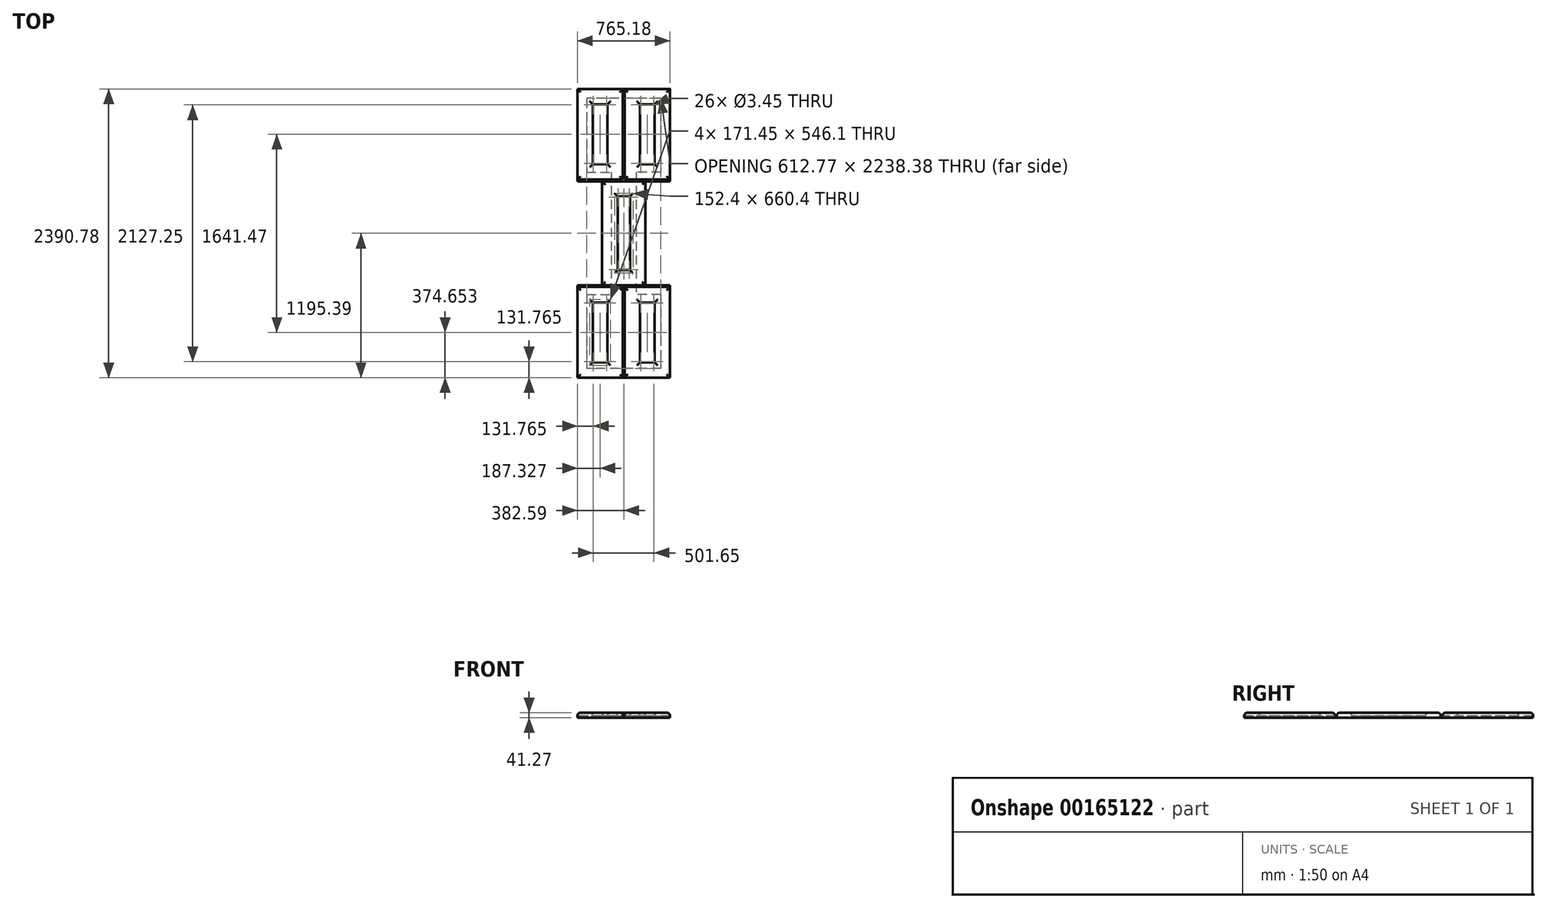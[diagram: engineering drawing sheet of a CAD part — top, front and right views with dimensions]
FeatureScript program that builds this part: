
annotation { "Feature Type Name" : "Feature", "Feature Type Description" : "" }
export const myFeature = defineFeature(function(context is Context, id is Id, definition is map)
    precondition{}
    {
        {
            var Q0;
            Q0=qCreatedBy(makeId("Top.planeOp"),FACE);
            var sketch = newSketch(context, id + "F0", { "sketchPlane" : qUnion([Q0])});
            skLineSegment(sketch, "E0", {"start": v(-179.39, 0) * mm, "end": v(179.39, 0) * mm, "construction": true});
            skLineSegment(sketch, "E1.left", {"start": v(-179.39, -430.21) * mm, "end": v(-179.39, 430.21) * mm});
            skLineSegment(sketch, "E1.right", {"start": v(179.39, -430.21) * mm, "end": v(179.39, 430.21) * mm});
            skLineSegment(sketch, "E2.bottom", {"start": v(-179.39, 430.21) * mm, "end": v(-382.59, 430.21) * mm});
            skLineSegment(sketch, "E2.top", {"start": v(382.59, 1195.39) * mm, "end": v(-382.59, 1195.39) * mm});
            skLineSegment(sketch, "E2.left", {"start": v(382.59, 430.21) * mm, "end": v(382.59, 1195.39) * mm});
            skLineSegment(sketch, "E2.right", {"start": v(-382.59, 430.21) * mm, "end": v(-382.59, 1195.39) * mm});
            skLineSegment(sketch, "E3", {"start": v(0, 0) * mm, "end": v(0, 1195.39) * mm, "construction": true});
            skLineSegment(sketch, "E4", {"start": v(-179.39, -430.21) * mm, "end": v(-382.59, -430.21) * mm});
            skLineSegment(sketch, "E5", {"start": v(179.39, 430.21) * mm, "end": v(382.59, 430.21) * mm});
            skLineSegment(sketch, "E6.bottom", {"start": v(382.59, -1195.39) * mm, "end": v(-382.59, -1195.39) * mm});
            skLineSegment(sketch, "E6.top", {"start": v(382.59, -430.21) * mm, "end": v(179.39, -430.21) * mm});
            skLineSegment(sketch, "E6.left", {"start": v(382.59, -1195.39) * mm, "end": v(382.59, -430.21) * mm});
            skLineSegment(sketch, "E6.right", {"start": v(-382.59, -1195.39) * mm, "end": v(-382.59, -430.21) * mm});
            skLineSegment(sketch, "E7", {"start": v(0, 0) * mm, "end": v(0, -1195.39) * mm, "construction": true});
            skLineSegment(sketch, "E8.bottom", {"start": v(-46.04, -300.04) * mm, "end": v(46.04, -300.04) * mm, "construction": true});
            skLineSegment(sketch, "E8.top", {"start": v(-46.04, 300.04) * mm, "end": v(46.04, 300.04) * mm, "construction": true});
            skLineSegment(sketch, "E8.left", {"start": v(-46.04, -300.04) * mm, "end": v(-46.04, 300.04) * mm, "construction": true});
            skLineSegment(sketch, "E8.right", {"start": v(46.04, -300.04) * mm, "end": v(46.04, 300.04) * mm, "construction": true});
            skPoint(sketch, "E8.middle", {"position": v(0, 0) * mm});
            skCircle(sketch, "E9", {"center": v(-46.04, 300.04) * mm, "radius": 1.73 * mm});
            skCircle(sketch, "E10", {"center": v(46.04, 300.04) * mm, "radius": 1.73 * mm});
            skCircle(sketch, "E11", {"center": v(46.04, 0) * mm, "radius": 1.73 * mm});
            skCircle(sketch, "E12", {"center": v(-46.04, 0) * mm, "radius": 1.73 * mm});
            skCircle(sketch, "E13", {"center": v(-46.04, -300.04) * mm, "radius": 1.73 * mm});
            skCircle(sketch, "E14", {"center": v(46.04, -300.04) * mm, "radius": 1.73 * mm});
            skLineSegment(sketch, "E15", {"start": v(195.26, 1195.39) * mm, "end": v(195.26, 820.74) * mm, "construction": true});
            skLineSegment(sketch, "E16", {"start": v(195.26, 820.74) * mm, "end": v(382.59, 820.74) * mm, "construction": true});
            skLineSegment(sketch, "E17", {"start": v(-195.26, 1195.39) * mm, "end": v(-195.26, 820.74) * mm, "construction": true});
            skLineSegment(sketch, "E18", {"start": v(-195.26, 820.74) * mm, "end": v(-382.59, 820.74) * mm, "construction": true});
            skLineSegment(sketch, "E19.bottom", {"start": v(250.83, 1063.62) * mm, "end": v(139.7, 1063.62) * mm, "construction": true});
            skLineSegment(sketch, "E19.top", {"start": v(250.83, 577.85) * mm, "end": v(139.7, 577.85) * mm, "construction": true});
            skLineSegment(sketch, "E19.left", {"start": v(250.83, 1063.62) * mm, "end": v(250.83, 577.85) * mm, "construction": true});
            skLineSegment(sketch, "E19.right", {"start": v(139.7, 1063.62) * mm, "end": v(139.7, 577.85) * mm, "construction": true});
            skPoint(sketch, "E19.middle", {"position": v(195.26, 820.74) * mm});
            skCircle(sketch, "E20", {"center": v(139.7, 1063.62) * mm, "radius": 1.73 * mm});
            skCircle(sketch, "E21", {"center": v(250.83, 1063.62) * mm, "radius": 1.73 * mm});
            skCircle(sketch, "E22", {"center": v(139.7, 577.85) * mm, "radius": 1.73 * mm});
            skCircle(sketch, "E23", {"center": v(250.83, 577.85) * mm, "radius": 1.73 * mm});
            skCircle(sketch, "E24", {"center": v(195.26, 820.74) * mm, "radius": 1.73 * mm});
            skLineSegment(sketch, "E25.bottom", {"start": v(-139.7, 1063.62) * mm, "end": v(-250.83, 1063.62) * mm, "construction": true});
            skLineSegment(sketch, "E25.top", {"start": v(-139.7, 577.85) * mm, "end": v(-250.83, 577.85) * mm, "construction": true});
            skLineSegment(sketch, "E25.left", {"start": v(-139.7, 1063.62) * mm, "end": v(-139.7, 577.85) * mm, "construction": true});
            skLineSegment(sketch, "E25.right", {"start": v(-250.83, 1063.62) * mm, "end": v(-250.83, 577.85) * mm, "construction": true});
            skPoint(sketch, "E25.middle", {"position": v(-195.26, 820.74) * mm});
            skCircle(sketch, "E26", {"center": v(-250.83, 1063.62) * mm, "radius": 1.73 * mm});
            skCircle(sketch, "E27", {"center": v(-139.7, 1063.62) * mm, "radius": 1.73 * mm});
            skCircle(sketch, "E28", {"center": v(-195.26, 820.74) * mm, "radius": 1.73 * mm});
            skCircle(sketch, "E29", {"center": v(-139.7, 577.85) * mm, "radius": 1.73 * mm});
            skCircle(sketch, "E30", {"center": v(-250.83, 577.85) * mm, "radius": 1.73 * mm});
            skLineSegment(sketch, "E31", {"start": v(-195.26, -1195.39) * mm, "end": v(-195.26, -820.74) * mm, "construction": true});
            skLineSegment(sketch, "E32", {"start": v(-195.26, -820.74) * mm, "end": v(-382.59, -820.74) * mm, "construction": true});
            skLineSegment(sketch, "E33", {"start": v(195.26, -1195.39) * mm, "end": v(195.26, -820.74) * mm, "construction": true});
            skLineSegment(sketch, "E34", {"start": v(195.26, -820.74) * mm, "end": v(382.59, -820.74) * mm, "construction": true});
            skLineSegment(sketch, "E35.bottom", {"start": v(-139.7, -577.85) * mm, "end": v(-250.83, -577.85) * mm, "construction": true});
            skLineSegment(sketch, "E35.top", {"start": v(-139.7, -1063.62) * mm, "end": v(-250.83, -1063.62) * mm, "construction": true});
            skLineSegment(sketch, "E35.left", {"start": v(-139.7, -577.85) * mm, "end": v(-139.7, -1063.62) * mm, "construction": true});
            skLineSegment(sketch, "E35.right", {"start": v(-250.83, -577.85) * mm, "end": v(-250.83, -1063.62) * mm, "construction": true});
            skPoint(sketch, "E35.middle", {"position": v(-195.26, -820.74) * mm});
            skLineSegment(sketch, "E36.bottom", {"start": v(139.7, -577.85) * mm, "end": v(250.82, -577.85) * mm, "construction": true});
            skLineSegment(sketch, "E36.top", {"start": v(139.7, -1063.62) * mm, "end": v(250.82, -1063.62) * mm, "construction": true});
            skLineSegment(sketch, "E36.left", {"start": v(139.7, -577.85) * mm, "end": v(139.7, -1063.62) * mm, "construction": true});
            skLineSegment(sketch, "E36.right", {"start": v(250.82, -577.85) * mm, "end": v(250.82, -1063.62) * mm, "construction": true});
            skPoint(sketch, "E36.middle", {"position": v(195.26, -820.74) * mm});
            skCircle(sketch, "E37", {"center": v(-250.83, -577.85) * mm, "radius": 1.73 * mm});
            skCircle(sketch, "E38", {"center": v(-139.7, -577.85) * mm, "radius": 1.73 * mm});
            skCircle(sketch, "E39", {"center": v(-195.26, -820.74) * mm, "radius": 1.73 * mm});
            skCircle(sketch, "E40", {"center": v(-139.7, -1063.62) * mm, "radius": 1.73 * mm});
            skCircle(sketch, "E41", {"center": v(-250.83, -1063.62) * mm, "radius": 1.73 * mm});
            skCircle(sketch, "E42", {"center": v(139.7, -1063.62) * mm, "radius": 1.73 * mm});
            skCircle(sketch, "E43", {"center": v(250.82, -1063.62) * mm, "radius": 1.73 * mm});
            skCircle(sketch, "E44", {"center": v(195.26, -820.74) * mm, "radius": 1.73 * mm});
            skCircle(sketch, "E45", {"center": v(139.7, -577.85) * mm, "radius": 1.73 * mm});
            skCircle(sketch, "E46", {"center": v(250.82, -577.85) * mm, "radius": 1.73 * mm});
            skSolve(sketch);
        }
        {
            var Q0;
            Q0=qSketchRegion(id+"F0",true);
            extrude(context, id + "F1", {"entities" : qUnion([Q0]), "depth" : 15.88 * mm});
        }
        {
            var Q0;
            Q0=makeQuery(id+"F1.opExtrude","CAP_FACE",FACE,{"disambiguationData":[OSD([sQuery(id+"F0.wireOp",EDGE,"E1.left"),sQuery(id+"F0.wireOp",EDGE,"E1.right"),sQuery(id+"F0.wireOp",EDGE,"E2.bottom"),sQuery(id+"F0.wireOp",EDGE,"E2.top"),sQuery(id+"F0.wireOp",EDGE,"E2.left"),sQuery(id+"F0.wireOp",EDGE,"E2.right"),sQuery(id+"F0.wireOp",EDGE,"E4"),sQuery(id+"F0.wireOp",EDGE,"E5"),sQuery(id+"F0.wireOp",EDGE,"E6.bottom"),sQuery(id+"F0.wireOp",EDGE,"E6.top"),sQuery(id+"F0.wireOp",EDGE,"E6.left"),sQuery(id+"F0.wireOp",EDGE,"E6.right"),sQuery(id+"F0.wireOp",EDGE,"E9"),sQuery(id+"F0.wireOp",EDGE,"E10"),sQuery(id+"F0.wireOp",EDGE,"E11"),sQuery(id+"F0.wireOp",EDGE,"E12"),sQuery(id+"F0.wireOp",EDGE,"E13"),sQuery(id+"F0.wireOp",EDGE,"E14"),sQuery(id+"F0.wireOp",EDGE,"E20"),sQuery(id+"F0.wireOp",EDGE,"E21"),sQuery(id+"F0.wireOp",EDGE,"E22"),sQuery(id+"F0.wireOp",EDGE,"E23"),sQuery(id+"F0.wireOp",EDGE,"E24"),sQuery(id+"F0.wireOp",EDGE,"E26"),sQuery(id+"F0.wireOp",EDGE,"E27"),sQuery(id+"F0.wireOp",EDGE,"E28"),sQuery(id+"F0.wireOp",EDGE,"E29"),sQuery(id+"F0.wireOp",EDGE,"E30"),sQuery(id+"F0.wireOp",EDGE,"E37"),sQuery(id+"F0.wireOp",EDGE,"E38"),sQuery(id+"F0.wireOp",EDGE,"E39"),sQuery(id+"F0.wireOp",EDGE,"E40"),sQuery(id+"F0.wireOp",EDGE,"E41"),sQuery(id+"F0.wireOp",EDGE,"E42"),sQuery(id+"F0.wireOp",EDGE,"E43"),sQuery(id+"F0.wireOp",EDGE,"E44"),sQuery(id+"F0.wireOp",EDGE,"E45"),sQuery(id+"F0.wireOp",EDGE,"E46")])],"isStart":false});
            var sketch = newSketch(context, id + "F2", { "sketchPlane" : qUnion([Q0])});
            skLineSegment(sketch, "E47.bottom", {"start": v(-139.7, 1063.62) * mm, "end": v(-250.82, 1063.62) * mm, "construction": true});
            skLineSegment(sketch, "E47.top", {"start": v(-139.7, 577.85) * mm, "end": v(-250.82, 577.85) * mm, "construction": true});
            skLineSegment(sketch, "E47.left", {"start": v(-139.7, 1063.62) * mm, "end": v(-139.7, 577.85) * mm, "construction": true});
            skLineSegment(sketch, "E47.right", {"start": v(-250.82, 1063.62) * mm, "end": v(-250.82, 577.85) * mm, "construction": true});
            skPoint(sketch, "E47.middle", {"position": v(-195.26, 820.74) * mm});
            skLineSegment(sketch, "E48.bottom", {"start": v(-134.94, 1068.39) * mm, "end": v(-255.59, 1068.39) * mm});
            skLineSegment(sketch, "E48.top", {"start": v(-134.94, 573.09) * mm, "end": v(-255.59, 573.09) * mm});
            skLineSegment(sketch, "E48.left", {"start": v(-134.94, 1068.39) * mm, "end": v(-134.94, 573.09) * mm});
            skLineSegment(sketch, "E48.right", {"start": v(-255.59, 1068.39) * mm, "end": v(-255.59, 573.09) * mm});
            skLineSegment(sketch, "E49", {"start": v(-139.7, 1063.62) * mm, "end": v(-139.7, 1068.39) * mm, "construction": true});
            skLineSegment(sketch, "E50", {"start": v(-139.7, 1063.62) * mm, "end": v(-134.94, 1063.62) * mm, "construction": true});
            skLineSegment(sketch, "E51.top", {"start": v(-382.59, 430.21) * mm, "end": v(382.59, 430.21) * mm});
            skLineSegment(sketch, "E51.left", {"start": v(-382.59, 444.5) * mm, "end": v(-382.59, 430.21) * mm, "construction": true});
            skLineSegment(sketch, "E51.right", {"start": v(382.59, 444.5) * mm, "end": v(382.59, 430.21) * mm, "construction": true});
            skLineSegment(sketch, "E52.bottom", {"start": v(-6.35, 1195.39) * mm, "end": v(6.35, 1195.39) * mm, "construction": true});
            skLineSegment(sketch, "E52.top", {"start": v(-6.35, 444.5) * mm, "end": v(6.35, 444.5) * mm, "construction": true});
            skLineSegment(sketch, "E52.left", {"start": v(-6.35, 1195.39) * mm, "end": v(-6.35, 444.5) * mm});
            skLineSegment(sketch, "E52.right", {"start": v(6.35, 1195.39) * mm, "end": v(6.35, 444.5) * mm});
            skLineSegment(sketch, "E53", {"start": v(-382.59, 444.5) * mm, "end": v(-6.35, 444.5) * mm});
            skLineSegment(sketch, "E54", {"start": v(6.35, 444.5) * mm, "end": v(382.59, 444.5) * mm});
            skLineSegment(sketch, "E55.bottom", {"start": v(250.83, 1063.62) * mm, "end": v(139.7, 1063.62) * mm, "construction": true});
            skLineSegment(sketch, "E55.top", {"start": v(250.83, 577.85) * mm, "end": v(139.7, 577.85) * mm, "construction": true});
            skLineSegment(sketch, "E55.left", {"start": v(250.83, 1063.62) * mm, "end": v(250.83, 577.85) * mm, "construction": true});
            skLineSegment(sketch, "E55.right", {"start": v(139.7, 1063.62) * mm, "end": v(139.7, 577.85) * mm, "construction": true});
            skPoint(sketch, "E55.middle", {"position": v(195.26, 820.74) * mm});
            skLineSegment(sketch, "E56.bottom", {"start": v(134.94, 1068.39) * mm, "end": v(255.59, 1068.39) * mm});
            skLineSegment(sketch, "E56.top", {"start": v(134.94, 573.09) * mm, "end": v(255.59, 573.09) * mm});
            skLineSegment(sketch, "E56.left", {"start": v(134.94, 1068.39) * mm, "end": v(134.94, 573.09) * mm});
            skLineSegment(sketch, "E56.right", {"start": v(255.59, 1068.39) * mm, "end": v(255.59, 573.09) * mm});
            skLineSegment(sketch, "E57.bottom", {"start": v(46.04, 300.04) * mm, "end": v(-46.04, 300.04) * mm, "construction": true});
            skLineSegment(sketch, "E57.top", {"start": v(46.04, -300.04) * mm, "end": v(-46.04, -300.04) * mm, "construction": true});
            skLineSegment(sketch, "E57.left", {"start": v(46.04, 300.04) * mm, "end": v(46.04, -300.04) * mm, "construction": true});
            skLineSegment(sketch, "E57.right", {"start": v(-46.04, 300.04) * mm, "end": v(-46.04, -300.04) * mm, "construction": true});
            skPoint(sketch, "E57.middle", {"position": v(0, 0) * mm});
            skLineSegment(sketch, "E58.bottom", {"start": v(50.8, 304.8) * mm, "end": v(-50.8, 304.8) * mm});
            skLineSegment(sketch, "E58.top", {"start": v(50.8, -304.8) * mm, "end": v(-50.8, -304.8) * mm});
            skLineSegment(sketch, "E58.left", {"start": v(50.8, 304.8) * mm, "end": v(50.8, -304.8) * mm});
            skLineSegment(sketch, "E58.right", {"start": v(-50.8, 304.8) * mm, "end": v(-50.8, -304.8) * mm});
            skLineSegment(sketch, "E59", {"start": v(46.04, 300.04) * mm, "end": v(46.04, 304.8) * mm, "construction": true});
            skLineSegment(sketch, "E60", {"start": v(46.04, 300.04) * mm, "end": v(50.8, 300.04) * mm, "construction": true});
            skLineSegment(sketch, "E61.bottom", {"start": v(-382.59, -430.21) * mm, "end": v(382.59, -430.21) * mm});
            skLineSegment(sketch, "E61.left", {"start": v(-382.59, -430.21) * mm, "end": v(-382.59, -444.5) * mm, "construction": true});
            skLineSegment(sketch, "E61.right", {"start": v(382.59, -430.21) * mm, "end": v(382.59, -444.5) * mm, "construction": true});
            skLineSegment(sketch, "E62.bottom", {"start": v(-6.35, -444.5) * mm, "end": v(6.35, -444.5) * mm, "construction": true});
            skLineSegment(sketch, "E62.top", {"start": v(-6.35, -1195.39) * mm, "end": v(6.35, -1195.39) * mm, "construction": true});
            skLineSegment(sketch, "E62.left", {"start": v(-6.35, -444.5) * mm, "end": v(-6.35, -1195.39) * mm});
            skLineSegment(sketch, "E62.right", {"start": v(6.35, -444.5) * mm, "end": v(6.35, -1195.39) * mm});
            skLineSegment(sketch, "E63", {"start": v(-382.59, -444.5) * mm, "end": v(-6.35, -444.5) * mm});
            skLineSegment(sketch, "E64", {"start": v(382.59, -444.5) * mm, "end": v(6.35, -444.5) * mm});
            skLineSegment(sketch, "E65.bottom", {"start": v(-134.94, -573.09) * mm, "end": v(-255.59, -573.09) * mm});
            skLineSegment(sketch, "E65.top", {"start": v(-134.94, -1068.39) * mm, "end": v(-255.59, -1068.39) * mm});
            skLineSegment(sketch, "E65.left", {"start": v(-134.94, -573.09) * mm, "end": v(-134.94, -1068.39) * mm});
            skLineSegment(sketch, "E65.right", {"start": v(-255.59, -573.09) * mm, "end": v(-255.59, -1068.39) * mm});
            skPoint(sketch, "E65.middle", {"position": v(-195.26, -820.74) * mm});
            skLineSegment(sketch, "E66.bottom", {"start": v(134.94, -573.09) * mm, "end": v(255.59, -573.09) * mm});
            skLineSegment(sketch, "E66.top", {"start": v(134.94, -1068.39) * mm, "end": v(255.59, -1068.39) * mm});
            skLineSegment(sketch, "E66.left", {"start": v(134.94, -573.09) * mm, "end": v(134.94, -1068.39) * mm});
            skLineSegment(sketch, "E66.right", {"start": v(255.59, -573.09) * mm, "end": v(255.59, -1068.39) * mm});
            skPoint(sketch, "E66.middle", {"position": v(195.26, -820.74) * mm});
            skSolve(sketch);
        }
        {
            var Q0;
            Q0=makeQuery(id+"F2.imprint","IMPRINT",FACE,{"disambiguationData":[TD([[makeQuery(id+"F2.imprint","IMPRINT",EDGE,{"derivedFrom":sQuery(id+"F2.wireOp",EDGE,"E48.bottom")}),-1.0]])]});
            var Q1;
            {var subQ1=sQuery(id+"F2.wireOp",EDGE,"E52.right");Q1=makeQuery(id+"F2.imprint","IMPRINT",FACE,{"disambiguationData":[TD([[makeQuery(id+"F2.imprint","IMPRINT",EDGE,{"derivedFrom":subQ1}),1.0]])]});}
            var Q2;
            {var subQ3=sQuery(id+"F2.wireOp",EDGE,"E62.left");Q2=makeQuery(id+"F2.imprint","IMPRINT",FACE,{"disambiguationData":[TD([[makeQuery(id+"F2.imprint","IMPRINT",EDGE,{"derivedFrom":subQ3}),-1.0]])]});}
            var Q3;
            {var subQ1=sQuery(id+"F2.wireOp",EDGE,"E62.right");Q3=makeQuery(id+"F2.imprint","IMPRINT",FACE,{"disambiguationData":[TD([[makeQuery(id+"F2.imprint","IMPRINT",EDGE,{"derivedFrom":subQ1}),1.0]])]});}
            var Q4;
            Q4=makeQuery(id+"F2.imprint","IMPRINT",FACE,{"disambiguationData":[TD([[makeQuery(id+"F2.imprint","IMPRINT",EDGE,{"derivedFrom":sQuery(id+"F2.wireOp",EDGE,"E58.bottom")}),-1.0]])]});
            extrude(context, id + "F3", {"entities" : qUnion([Q0, Q1, Q2, Q3, Q4]), "operationType" : NewBodyOperationType.ADD, "depth" : 25.4 * mm});
        }
        {
            var Q0;
            Q0=makeQuery(id+"F3.opExtrude","CAP_FACE",FACE,{"disambiguationData":[OSD([sQuery(id+"F0.wireOp",EDGE,"E2.top"),sQuery(id+"F0.wireOp",EDGE,"E2.right"),sQuery(id+"F2.wireOp",EDGE,"E48.bottom"),sQuery(id+"F2.wireOp",EDGE,"E48.top"),sQuery(id+"F2.wireOp",EDGE,"E48.left"),sQuery(id+"F2.wireOp",EDGE,"E48.right"),sQuery(id+"F2.wireOp",EDGE,"E52.left"),sQuery(id+"F2.wireOp",EDGE,"E53")])],"isStart":false});
            var Q1;
            Q1=makeQuery(id+"F3.opExtrude","CAP_FACE",FACE,{"disambiguationData":[OSD([sQuery(id+"F0.wireOp",EDGE,"E2.top"),sQuery(id+"F0.wireOp",EDGE,"E2.left"),sQuery(id+"F2.wireOp",EDGE,"E52.right"),sQuery(id+"F2.wireOp",EDGE,"E54"),sQuery(id+"F2.wireOp",EDGE,"E56.bottom"),sQuery(id+"F2.wireOp",EDGE,"E56.top"),sQuery(id+"F2.wireOp",EDGE,"E56.left"),sQuery(id+"F2.wireOp",EDGE,"E56.right")])],"isStart":false});
            var Q2;
            Q2=makeQuery(id+"F3.opExtrude","CAP_FACE",FACE,{"disambiguationData":[OSD([sQuery(id+"F0.wireOp",EDGE,"E1.left"),sQuery(id+"F0.wireOp",EDGE,"E1.right"),sQuery(id+"F2.wireOp",EDGE,"E51.top"),sQuery(id+"F2.wireOp",EDGE,"E58.bottom"),sQuery(id+"F2.wireOp",EDGE,"E58.top"),sQuery(id+"F2.wireOp",EDGE,"E58.left"),sQuery(id+"F2.wireOp",EDGE,"E58.right"),sQuery(id+"F2.wireOp",EDGE,"E61.bottom")])],"isStart":false});
            var Q3;
            Q3=makeQuery(id+"F3.opExtrude","CAP_FACE",FACE,{"disambiguationData":[OSD([sQuery(id+"F0.wireOp",EDGE,"E6.bottom"),sQuery(id+"F0.wireOp",EDGE,"E6.left"),sQuery(id+"F2.wireOp",EDGE,"E62.right"),sQuery(id+"F2.wireOp",EDGE,"E64"),sQuery(id+"F2.wireOp",EDGE,"E66.bottom"),sQuery(id+"F2.wireOp",EDGE,"E66.top"),sQuery(id+"F2.wireOp",EDGE,"E66.left"),sQuery(id+"F2.wireOp",EDGE,"E66.right")])],"isStart":false});
            var Q4;
            Q4=makeQuery(id+"F3.opExtrude","CAP_FACE",FACE,{"disambiguationData":[OSD([sQuery(id+"F0.wireOp",EDGE,"E6.bottom"),sQuery(id+"F0.wireOp",EDGE,"E6.right"),sQuery(id+"F2.wireOp",EDGE,"E62.left"),sQuery(id+"F2.wireOp",EDGE,"E63"),sQuery(id+"F2.wireOp",EDGE,"E65.bottom"),sQuery(id+"F2.wireOp",EDGE,"E65.top"),sQuery(id+"F2.wireOp",EDGE,"E65.left"),sQuery(id+"F2.wireOp",EDGE,"E65.right")])],"isStart":false});
            fillet(context, id + "F4", {"entities" : qUnion([Q0, Q1, Q2, Q3, Q4]), "radius" : 25.4 * mm, "tangentPropagation" : true, "allowEdgeOverflow" : false});
        }
        {
            var Q0;
            Q0=makeQuery(id+"F1.opExtrude","CAP_FACE",FACE,{"disambiguationData":[OSD([sQuery(id+"F0.wireOp",EDGE,"E1.left"),sQuery(id+"F0.wireOp",EDGE,"E1.right"),sQuery(id+"F0.wireOp",EDGE,"E2.bottom"),sQuery(id+"F0.wireOp",EDGE,"E2.top"),sQuery(id+"F0.wireOp",EDGE,"E2.left"),sQuery(id+"F0.wireOp",EDGE,"E2.right"),sQuery(id+"F0.wireOp",EDGE,"E4"),sQuery(id+"F0.wireOp",EDGE,"E5"),sQuery(id+"F0.wireOp",EDGE,"E6.bottom"),sQuery(id+"F0.wireOp",EDGE,"E6.top"),sQuery(id+"F0.wireOp",EDGE,"E6.left"),sQuery(id+"F0.wireOp",EDGE,"E6.right"),sQuery(id+"F0.wireOp",EDGE,"E9"),sQuery(id+"F0.wireOp",EDGE,"E10"),sQuery(id+"F0.wireOp",EDGE,"E11"),sQuery(id+"F0.wireOp",EDGE,"E12"),sQuery(id+"F0.wireOp",EDGE,"E13"),sQuery(id+"F0.wireOp",EDGE,"E14"),sQuery(id+"F0.wireOp",EDGE,"E20"),sQuery(id+"F0.wireOp",EDGE,"E21"),sQuery(id+"F0.wireOp",EDGE,"E22"),sQuery(id+"F0.wireOp",EDGE,"E23"),sQuery(id+"F0.wireOp",EDGE,"E24"),sQuery(id+"F0.wireOp",EDGE,"E26"),sQuery(id+"F0.wireOp",EDGE,"E27"),sQuery(id+"F0.wireOp",EDGE,"E28"),sQuery(id+"F0.wireOp",EDGE,"E29"),sQuery(id+"F0.wireOp",EDGE,"E30"),sQuery(id+"F0.wireOp",EDGE,"E37"),sQuery(id+"F0.wireOp",EDGE,"E38"),sQuery(id+"F0.wireOp",EDGE,"E39"),sQuery(id+"F0.wireOp",EDGE,"E40"),sQuery(id+"F0.wireOp",EDGE,"E41"),sQuery(id+"F0.wireOp",EDGE,"E42"),sQuery(id+"F0.wireOp",EDGE,"E43"),sQuery(id+"F0.wireOp",EDGE,"E44"),sQuery(id+"F0.wireOp",EDGE,"E45"),sQuery(id+"F0.wireOp",EDGE,"E46")])],"isStart":true});
            var Q1;
            Q1=makeQuery(id+"F1.opExtrude","SWEPT_BODY",BODY,{"disambiguationData":[OSD([sQuery(id+"F0.wireOp",EDGE,"E1.left"),sQuery(id+"F0.wireOp",EDGE,"E1.right"),sQuery(id+"F0.wireOp",EDGE,"E2.bottom"),sQuery(id+"F0.wireOp",EDGE,"E2.top"),sQuery(id+"F0.wireOp",EDGE,"E2.left"),sQuery(id+"F0.wireOp",EDGE,"E2.right"),sQuery(id+"F0.wireOp",EDGE,"E4"),sQuery(id+"F0.wireOp",EDGE,"E5"),sQuery(id+"F0.wireOp",EDGE,"E6.bottom"),sQuery(id+"F0.wireOp",EDGE,"E6.top"),sQuery(id+"F0.wireOp",EDGE,"E6.left"),sQuery(id+"F0.wireOp",EDGE,"E6.right"),sQuery(id+"F0.wireOp",EDGE,"E9"),sQuery(id+"F0.wireOp",EDGE,"E10"),sQuery(id+"F0.wireOp",EDGE,"E11"),sQuery(id+"F0.wireOp",EDGE,"E12"),sQuery(id+"F0.wireOp",EDGE,"E13"),sQuery(id+"F0.wireOp",EDGE,"E14"),sQuery(id+"F0.wireOp",EDGE,"E20"),sQuery(id+"F0.wireOp",EDGE,"E21"),sQuery(id+"F0.wireOp",EDGE,"E22"),sQuery(id+"F0.wireOp",EDGE,"E23"),sQuery(id+"F0.wireOp",EDGE,"E24"),sQuery(id+"F0.wireOp",EDGE,"E26"),sQuery(id+"F0.wireOp",EDGE,"E27"),sQuery(id+"F0.wireOp",EDGE,"E28"),sQuery(id+"F0.wireOp",EDGE,"E29"),sQuery(id+"F0.wireOp",EDGE,"E30"),sQuery(id+"F0.wireOp",EDGE,"E37"),sQuery(id+"F0.wireOp",EDGE,"E38"),sQuery(id+"F0.wireOp",EDGE,"E39"),sQuery(id+"F0.wireOp",EDGE,"E40"),sQuery(id+"F0.wireOp",EDGE,"E41"),sQuery(id+"F0.wireOp",EDGE,"E42"),sQuery(id+"F0.wireOp",EDGE,"E43"),sQuery(id+"F0.wireOp",EDGE,"E44"),sQuery(id+"F0.wireOp",EDGE,"E45"),sQuery(id+"F0.wireOp",EDGE,"E46")])]});
            shell(context, id + "F5", {"isHollow" : true, "entities" : qUnion([Q0]), "parts" : qUnion([Q1]), "thickness" : 1.59 * mm});
        }
        {
            var Q0;
            Q0=makeQuery(id+"F1.opExtrude","CAP_FACE",FACE,{"disambiguationData":[OSD([sQuery(id+"F0.wireOp",EDGE,"E1.left"),sQuery(id+"F0.wireOp",EDGE,"E1.right"),sQuery(id+"F0.wireOp",EDGE,"E2.bottom"),sQuery(id+"F0.wireOp",EDGE,"E2.top"),sQuery(id+"F0.wireOp",EDGE,"E2.left"),sQuery(id+"F0.wireOp",EDGE,"E2.right"),sQuery(id+"F0.wireOp",EDGE,"E4"),sQuery(id+"F0.wireOp",EDGE,"E5"),sQuery(id+"F0.wireOp",EDGE,"E6.bottom"),sQuery(id+"F0.wireOp",EDGE,"E6.top"),sQuery(id+"F0.wireOp",EDGE,"E6.left"),sQuery(id+"F0.wireOp",EDGE,"E6.right"),sQuery(id+"F0.wireOp",EDGE,"E9"),sQuery(id+"F0.wireOp",EDGE,"E10"),sQuery(id+"F0.wireOp",EDGE,"E11"),sQuery(id+"F0.wireOp",EDGE,"E12"),sQuery(id+"F0.wireOp",EDGE,"E13"),sQuery(id+"F0.wireOp",EDGE,"E14"),sQuery(id+"F0.wireOp",EDGE,"E20"),sQuery(id+"F0.wireOp",EDGE,"E21"),sQuery(id+"F0.wireOp",EDGE,"E22"),sQuery(id+"F0.wireOp",EDGE,"E23"),sQuery(id+"F0.wireOp",EDGE,"E24"),sQuery(id+"F0.wireOp",EDGE,"E26"),sQuery(id+"F0.wireOp",EDGE,"E27"),sQuery(id+"F0.wireOp",EDGE,"E28"),sQuery(id+"F0.wireOp",EDGE,"E29"),sQuery(id+"F0.wireOp",EDGE,"E30"),sQuery(id+"F0.wireOp",EDGE,"E37"),sQuery(id+"F0.wireOp",EDGE,"E38"),sQuery(id+"F0.wireOp",EDGE,"E39"),sQuery(id+"F0.wireOp",EDGE,"E40"),sQuery(id+"F0.wireOp",EDGE,"E41"),sQuery(id+"F0.wireOp",EDGE,"E42"),sQuery(id+"F0.wireOp",EDGE,"E43"),sQuery(id+"F0.wireOp",EDGE,"E44"),sQuery(id+"F0.wireOp",EDGE,"E45"),sQuery(id+"F0.wireOp",EDGE,"E46")])],"isStart":true});
            var sketch = newSketch(context, id + "F6", { "sketchPlane" : qUnion([Q0])});
            skLineSegment(sketch, "E67.bottom", {"start": v(306.39, -1119.19) * mm, "end": v(-306.39, -1119.19) * mm});
            skLineSegment(sketch, "E67.left", {"start": v(306.39, -1119.19) * mm, "end": v(306.39, -506.41) * mm});
            skLineSegment(sketch, "E67.right", {"start": v(-306.39, -1119.19) * mm, "end": v(-306.39, -506.41) * mm});
            skLineSegment(sketch, "E68.top", {"start": v(306.39, 1119.19) * mm, "end": v(-306.39, 1119.19) * mm});
            skLineSegment(sketch, "E68.left", {"start": v(306.39, 506.41) * mm, "end": v(306.39, 1119.19) * mm});
            skLineSegment(sketch, "E68.right", {"start": v(-306.39, 506.41) * mm, "end": v(-306.39, 1119.19) * mm});
            skLineSegment(sketch, "E69.bottom", {"start": v(306.39, 506.41) * mm, "end": v(382.59, 506.41) * mm, "construction": true});
            skLineSegment(sketch, "E69.top", {"start": v(306.39, 430.21) * mm, "end": v(382.59, 430.21) * mm, "construction": true});
            skLineSegment(sketch, "E69.left", {"start": v(306.39, 506.41) * mm, "end": v(306.39, 430.21) * mm, "construction": true});
            skLineSegment(sketch, "E69.right", {"start": v(382.59, 506.41) * mm, "end": v(382.59, 430.21) * mm, "construction": true});
            skLineSegment(sketch, "E70.bottom", {"start": v(-306.39, 1119.19) * mm, "end": v(-382.59, 1119.19) * mm, "construction": true});
            skLineSegment(sketch, "E70.top", {"start": v(-306.39, 1195.39) * mm, "end": v(-382.59, 1195.39) * mm, "construction": true});
            skLineSegment(sketch, "E70.left", {"start": v(-306.39, 1119.19) * mm, "end": v(-306.39, 1195.39) * mm, "construction": true});
            skLineSegment(sketch, "E70.right", {"start": v(-382.59, 1119.19) * mm, "end": v(-382.59, 1195.39) * mm, "construction": true});
            skLineSegment(sketch, "E71.bottom", {"start": v(-306.39, -1119.19) * mm, "end": v(-382.59, -1119.19) * mm, "construction": true});
            skLineSegment(sketch, "E71.top", {"start": v(-306.39, -1195.39) * mm, "end": v(-382.59, -1195.39) * mm, "construction": true});
            skLineSegment(sketch, "E71.left", {"start": v(-306.39, -1119.19) * mm, "end": v(-306.39, -1195.39) * mm, "construction": true});
            skLineSegment(sketch, "E71.right", {"start": v(-382.59, -1119.19) * mm, "end": v(-382.59, -1195.39) * mm, "construction": true});
            skLineSegment(sketch, "E72.bottom", {"start": v(306.39, -506.41) * mm, "end": v(382.59, -506.41) * mm, "construction": true});
            skLineSegment(sketch, "E72.top", {"start": v(306.39, -430.21) * mm, "end": v(382.59, -430.21) * mm, "construction": true});
            skLineSegment(sketch, "E72.left", {"start": v(306.39, -506.41) * mm, "end": v(306.39, -430.21) * mm, "construction": true});
            skLineSegment(sketch, "E72.right", {"start": v(382.59, -506.41) * mm, "end": v(382.59, -430.21) * mm, "construction": true});
            skLineSegment(sketch, "E73", {"start": v(306.39, -506.41) * mm, "end": v(103.19, -506.41) * mm});
            skLineSegment(sketch, "E74", {"start": v(-306.39, -506.41) * mm, "end": v(-103.19, -506.41) * mm});
            skLineSegment(sketch, "E75", {"start": v(306.39, 506.41) * mm, "end": v(103.19, 506.41) * mm});
            skLineSegment(sketch, "E76", {"start": v(-306.39, 506.41) * mm, "end": v(-103.19, 506.41) * mm});
            skLineSegment(sketch, "E77.bottom", {"start": v(103.19, -506.41) * mm, "end": v(-103.19, -506.41) * mm, "construction": true});
            skLineSegment(sketch, "E77.top", {"start": v(103.19, 506.41) * mm, "end": v(-103.19, 506.41) * mm, "construction": true});
            skLineSegment(sketch, "E77.left", {"start": v(103.19, -506.41) * mm, "end": v(103.19, 506.41) * mm});
            skLineSegment(sketch, "E77.right", {"start": v(-103.19, -506.41) * mm, "end": v(-103.19, 506.41) * mm});
            skLineSegment(sketch, "E78", {"start": v(179.39, 0) * mm, "end": v(103.19, 0) * mm, "construction": true});
            skLineSegment(sketch, "E79", {"start": v(-103.19, 0) * mm, "end": v(-179.39, 0) * mm, "construction": true});
            skSolve(sketch);
        }
        {
            var Q0;
            Q0=qSketchRegion(id+"F6",true);
            extrude(context, id + "F7", {"entities" : qUnion([Q0]), "operationType" : NewBodyOperationType.REMOVE, "oppositeDirection" : true, "depth" : 1.59 * mm});
        }
        {
            var Q0;
            {var subQ0=sQuery(id+"F0.wireOp",EDGE,"E22");var subQ1=sQuery(id+"F0.wireOp",EDGE,"E21");var subQ2=sQuery(id+"F0.wireOp",EDGE,"E23");var subQ3=sQuery(id+"F0.wireOp",EDGE,"E20");var subQ4=sQuery(id+"F0.wireOp",EDGE,"E24");var subQ5=sQuery(id+"F0.wireOp",EDGE,"E46");var subQ6=sQuery(id+"F0.wireOp",EDGE,"E45");var subQ7=sQuery(id+"F0.wireOp",EDGE,"E44");var subQ8=sQuery(id+"F0.wireOp",EDGE,"E43");var subQ9=sQuery(id+"F0.wireOp",EDGE,"E42");var subQ10=sQuery(id+"F0.wireOp",EDGE,"E41");var subQ11=sQuery(id+"F0.wireOp",EDGE,"E40");var subQ12=sQuery(id+"F0.wireOp",EDGE,"E39");var subQ13=sQuery(id+"F0.wireOp",EDGE,"E38");var subQ14=sQuery(id+"F0.wireOp",EDGE,"E37");var subQ15=sQuery(id+"F0.wireOp",EDGE,"E30");var subQ16=sQuery(id+"F0.wireOp",EDGE,"E29");var subQ17=sQuery(id+"F0.wireOp",EDGE,"E28");var subQ18=sQuery(id+"F0.wireOp",EDGE,"E27");var subQ19=sQuery(id+"F0.wireOp",EDGE,"E26");var subQ20=sQuery(id+"F0.wireOp",EDGE,"E14");var subQ21=sQuery(id+"F0.wireOp",EDGE,"E13");var subQ22=sQuery(id+"F0.wireOp",EDGE,"E12");var subQ23=sQuery(id+"F0.wireOp",EDGE,"E11");var subQ24=sQuery(id+"F0.wireOp",EDGE,"E10");var subQ25=sQuery(id+"F0.wireOp",EDGE,"E9");var subQ26=sQuery(id+"F0.wireOp",EDGE,"E6.right");var subQ27=sQuery(id+"F0.wireOp",EDGE,"E6.left");var subQ28=sQuery(id+"F0.wireOp",EDGE,"E6.top");var subQ29=sQuery(id+"F0.wireOp",EDGE,"E6.bottom");var subQ30=sQuery(id+"F0.wireOp",EDGE,"E5");var subQ31=sQuery(id+"F0.wireOp",EDGE,"E4");var subQ32=sQuery(id+"F0.wireOp",EDGE,"E2.right");var subQ33=sQuery(id+"F0.wireOp",EDGE,"E2.left");var subQ34=sQuery(id+"F0.wireOp",EDGE,"E2.top");var subQ35=sQuery(id+"F0.wireOp",EDGE,"E2.bottom");var subQ36=sQuery(id+"F0.wireOp",EDGE,"E1.right");var subQ37=sQuery(id+"F0.wireOp",EDGE,"E1.left");Q0=makeQuery(id+"F5.opShell","OFFSET_FACE",FACE,{"disambiguationData":[OSD([subQ37,subQ36,subQ35,subQ34,subQ33,subQ32,subQ31,subQ30,subQ29,subQ28,subQ27,subQ26,subQ25,subQ24,subQ23,subQ22,subQ21,subQ20,subQ3,subQ1,subQ0,subQ2,subQ4,subQ19,subQ18,subQ17,subQ16,subQ15,subQ14,subQ13,subQ12,subQ11,subQ10,subQ9,subQ8,subQ7,subQ6,subQ5]),TDD([makeQuery(id+"F3.boolean.opBoolean","SPLIT",FACE,{"disambiguationData":[TD([makeQuery(id+"F1.opExtrude","SWEPT_FACE",FACE,{"disambiguationData":[OSD([subQ3])]})])],"derivedFrom":makeQuery(id+"F1.opExtrude","CAP_FACE",FACE,{"disambiguationData":[OSD([subQ37,subQ36,subQ35,subQ34,subQ33,subQ32,subQ31,subQ30,subQ29,subQ28,subQ27,subQ26,subQ25,subQ24,subQ23,subQ22,subQ21,subQ20,subQ3,subQ1,subQ0,subQ2,subQ4,subQ19,subQ18,subQ17,subQ16,subQ15,subQ14,subQ13,subQ12,subQ11,subQ10,subQ9,subQ8,subQ7,subQ6,subQ5])],"isStart":false})})])]});}
            var sketch = newSketch(context, id + "F8", { "sketchPlane" : qUnion([Q0])});
            skLineSegment(sketch, "E80.bottom", {"start": v(133.3, 1070.03) * mm, "end": v(257.23, 1070.03) * mm});
            skLineSegment(sketch, "E80.top", {"start": v(133.3, 571.45) * mm, "end": v(257.23, 571.45) * mm});
            skLineSegment(sketch, "E80.left", {"start": v(133.3, 1070.03) * mm, "end": v(133.3, 571.45) * mm});
            skLineSegment(sketch, "E80.right", {"start": v(257.23, 1070.03) * mm, "end": v(257.23, 571.45) * mm});
            skLineSegment(sketch, "E81.bottom", {"start": v(-257.23, 1070.03) * mm, "end": v(-133.3, 1070.03) * mm});
            skLineSegment(sketch, "E81.top", {"start": v(-257.23, 571.45) * mm, "end": v(-133.3, 571.45) * mm});
            skLineSegment(sketch, "E81.left", {"start": v(-257.23, 1070.03) * mm, "end": v(-257.23, 571.45) * mm});
            skLineSegment(sketch, "E81.right", {"start": v(-133.3, 1070.03) * mm, "end": v(-133.3, 571.45) * mm});
            skLineSegment(sketch, "E82.bottom", {"start": v(-52.44, 306.44) * mm, "end": v(52.44, 306.44) * mm});
            skLineSegment(sketch, "E82.top", {"start": v(-52.44, -306.44) * mm, "end": v(52.44, -306.44) * mm});
            skLineSegment(sketch, "E82.left", {"start": v(-52.44, 306.44) * mm, "end": v(-52.44, -306.44) * mm});
            skLineSegment(sketch, "E82.right", {"start": v(52.44, 306.44) * mm, "end": v(52.44, -306.44) * mm});
            skLineSegment(sketch, "E83.bottom", {"start": v(-257.23, -571.45) * mm, "end": v(-133.3, -571.45) * mm});
            skLineSegment(sketch, "E83.top", {"start": v(-257.23, -1070.03) * mm, "end": v(-133.3, -1070.03) * mm});
            skLineSegment(sketch, "E83.left", {"start": v(-257.23, -571.45) * mm, "end": v(-257.23, -1070.03) * mm});
            skLineSegment(sketch, "E83.right", {"start": v(-133.3, -571.45) * mm, "end": v(-133.3, -1070.03) * mm});
            skLineSegment(sketch, "E84.bottom", {"start": v(133.3, -571.45) * mm, "end": v(257.23, -571.45) * mm});
            skLineSegment(sketch, "E84.top", {"start": v(133.3, -1070.03) * mm, "end": v(257.23, -1070.03) * mm});
            skLineSegment(sketch, "E84.left", {"start": v(133.3, -571.45) * mm, "end": v(133.3, -1070.03) * mm});
            skLineSegment(sketch, "E84.right", {"start": v(257.23, -571.45) * mm, "end": v(257.23, -1070.03) * mm});
            skSolve(sketch);
        }
        {
            var Q0;
            Q0 = qSketchRegion(id + "F8", true);
            var Q1;
            {var subQ0=sQuery(id+"F0.wireOp",EDGE,"E22");Q1=makeQuery(id+"F7.boolean.opBoolean","COPY",FACE,{"disambiguationData":[TD([makeQuery(id+"F1.opExtrude","SWEPT_FACE",FACE,{"disambiguationData":[OSD([subQ0])]})])],"derivedFrom":makeQuery(id+"F7.opExtrude","CAP_FACE",FACE,{"disambiguationData":[OSD([sQuery(id+"F6.wireOp",EDGE,"E67.bottom"),sQuery(id+"F6.wireOp",EDGE,"E67.left"),sQuery(id+"F6.wireOp",EDGE,"E67.right"),sQuery(id+"F6.wireOp",EDGE,"E68.top"),sQuery(id+"F6.wireOp",EDGE,"E68.left"),sQuery(id+"F6.wireOp",EDGE,"E68.right"),sQuery(id+"F6.wireOp",EDGE,"E73"),sQuery(id+"F6.wireOp",EDGE,"E74"),sQuery(id+"F6.wireOp",EDGE,"E75"),sQuery(id+"F6.wireOp",EDGE,"E76"),sQuery(id+"F6.wireOp",EDGE,"E77.left"),sQuery(id+"F6.wireOp",EDGE,"E77.right")])],"isStart":false})});}
            extrude(context, id + "F9", {"entities" : qUnion([Q0]), "operationType" : NewBodyOperationType.REMOVE, "endBound" : BoundingType.UP_TO_SURFACE, "endBoundEntityFace" : qUnion([Q1]), "depth" : 25.4 * mm});
        }
    });
